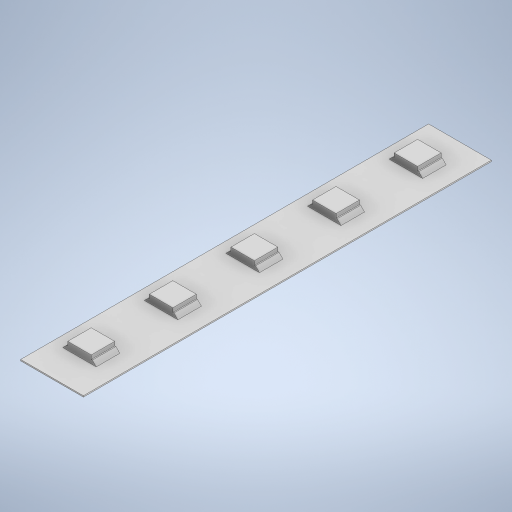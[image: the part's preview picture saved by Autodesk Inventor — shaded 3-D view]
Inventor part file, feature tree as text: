
AUTODESK INVENTOR PART (.ipt)
format: ipt  version: 2023 (Build 270158000, 158)  size: 342,528 bytes
history: native  units: in
note: dims shown in document units (in); Inventor stores cm internally (conversion verified against a paired STEP export)
features: extrude x3, sketch x2, chamfer x1
ambient origin geometry x8: Origin, YZ Plane, XZ Plane, XY Plane, X Axis, Y Axis, Z Axis, Center Point
bodies: Solid1 (feature_tree)
feature tree (6):
  extrude  "Extrusion1"  Depth=3.25in
  sketch  "Sketch2"  dims[d2=0.01in d3=0.0in d4=0.1875in d5=0.1875in d6=0.25in d7=0.125in d8=0.1875in d9=0.1875in d10=0.4625in d11=0.125in d12=0.1875in d13=0.1875in d14=0.1875in d15=0.1875in d16=0.1875in d17=0.1875in d18=0.4625in d19=0.4625in d20=0.4625in d21=0.125in d22=0.04in d23=0.04in d24=0.0625in d25=0.0in d26=0.0312in d27=0.0in d28=0.0312in d29=0.125in d30=45.0deg d31=0.1875in d32=0.1875in d33=0.1875in d34=0.1875in]
  extrude  "Extrusion2"  Depth=0.1875in
  extrude  "Extrusion3"  Depth=0.1875in
  chamfer  "Chamfer1"  Distance=0.25in
  sketch  "Sketch1"  dims[d0=0.5in d1=3.25in]
